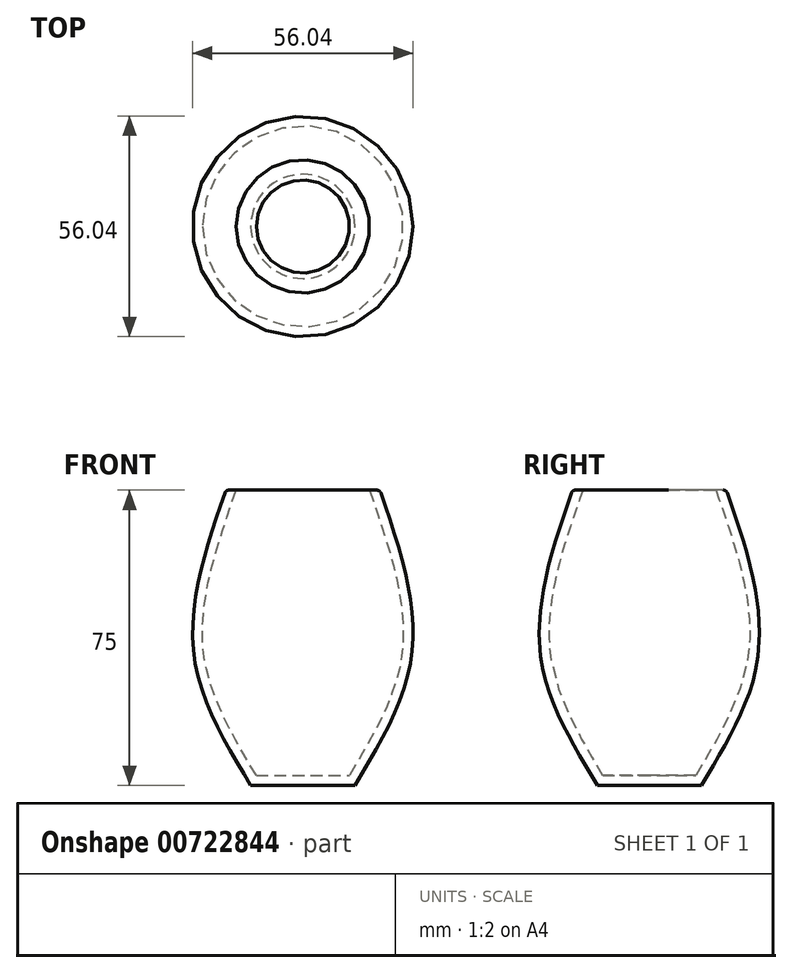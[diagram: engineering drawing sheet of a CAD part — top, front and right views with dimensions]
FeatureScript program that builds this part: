
annotation { "Feature Type Name" : "Feature", "Feature Type Description" : "" }
export const myFeature = defineFeature(function(context is Context, id is Id, definition is map)
    precondition{}
    {
        {
            var Q0;
            Q0=qCreatedBy(makeId("Top.planeOp"),FACE);
            var sketch = newSketch(context, id + "F0", { "sketchPlane" : qUnion([Q0])});
            skCircle(sketch, "E0", {"center": v(0, 0) * mm, "radius": 13.24 * mm});
            skSolve(sketch);
        }
        {
            var Q0;
            Q0=qCreatedBy(makeId("Top.planeOp"),FACE);
            cPlane(context, id + "F1", {"entities" : qUnion([Q0]), "cplaneType" : CPlaneType.OFFSET, "offset" : 32 * mm, "width" : 150 * mm, "height" : 150 * mm});
        }
        {
            var Q0;
            Q0=qCreatedBy(id+"F1.planeOp",FACE);
            cPlane(context, id + "F2", {"entities" : qUnion([Q0]), "cplaneType" : CPlaneType.OFFSET, "offset" : 43 * mm, "width" : 150 * mm, "height" : 150 * mm});
        }
        {
            var Q0;
            Q0=qCreatedBy(id+"F1.planeOp",FACE);
            var sketch = newSketch(context, id + "F3", { "sketchPlane" : qUnion([Q0])});
            skCircle(sketch, "E1", {"center": v(0, 0) * mm, "radius": 27.52 * mm});
            skSolve(sketch);
        }
        {
            var Q0;
            Q0=qCreatedBy(id+"F2.planeOp",FACE);
            var sketch = newSketch(context, id + "F4", { "sketchPlane" : qUnion([Q0])});
            skCircle(sketch, "E2", {"center": v(0, 0) * mm, "radius": 19.58 * mm});
            skSolve(sketch);
        }
        {
            var Q0;
            Q0=makeQuery(id+"F0.imprint","IMPRINT",FACE,{"disambiguationData":[TD([[makeQuery(id+"F0.imprint","IMPRINT",EDGE,{"derivedFrom":sQuery(id+"F0.wireOp",EDGE,"E0")}),1.0]])]});
            var Q1;
            Q1=makeQuery(id+"F3.imprint","IMPRINT",FACE,{"disambiguationData":[TD([[makeQuery(id+"F3.imprint","IMPRINT",EDGE,{"derivedFrom":sQuery(id+"F3.wireOp",EDGE,"E1")}),1.0]])]});
            var Q2;
            Q2=makeQuery(id+"F4.imprint","IMPRINT",FACE,{"disambiguationData":[TD([[makeQuery(id+"F4.imprint","IMPRINT",EDGE,{"derivedFrom":sQuery(id+"F4.wireOp",EDGE,"E2")}),1.0]])]});
            loft(context, id + "F5", {"sheetProfilesArray" : [{ "sheetProfileEntities" : qUnion([Q0]) }, { "sheetProfileEntities" : qUnion([Q1]) }, { "sheetProfileEntities" : qUnion([Q2]) }]});
        }
        {
            var Q0;
            Q0=makeQuery(id+"F5.opLoft","CAP_FACE",FACE,{"disambiguationData":[OSD([makeQuery(id+"F4.imprint","IMPRINT",FACE,{"disambiguationData":[TD([[makeQuery(id+"F4.imprint","IMPRINT",EDGE,{"derivedFrom":sQuery(id+"F4.wireOp",EDGE,"E2")}),1.0]])]})])],"isStart":true});
            shell(context, id + "F6", {"entities" : qUnion([Q0]), "thickness" : 2.5 * mm});
        }
        {
            var Q0;
            Q0=makeQuery(id+"F5.opLoft","MID_CAP_EDGE",EDGE,{"disambiguationData":[OSD([sQuery(id+"F4.wireOp",EDGE,"E2")])],"capPos":2.0});
            fillet(context, id + "F7", {"entities" : qUnion([Q0]), "radius" : 1 * mm, "tangentPropagation" : true, "allowEdgeOverflow" : false});
        }
    });
